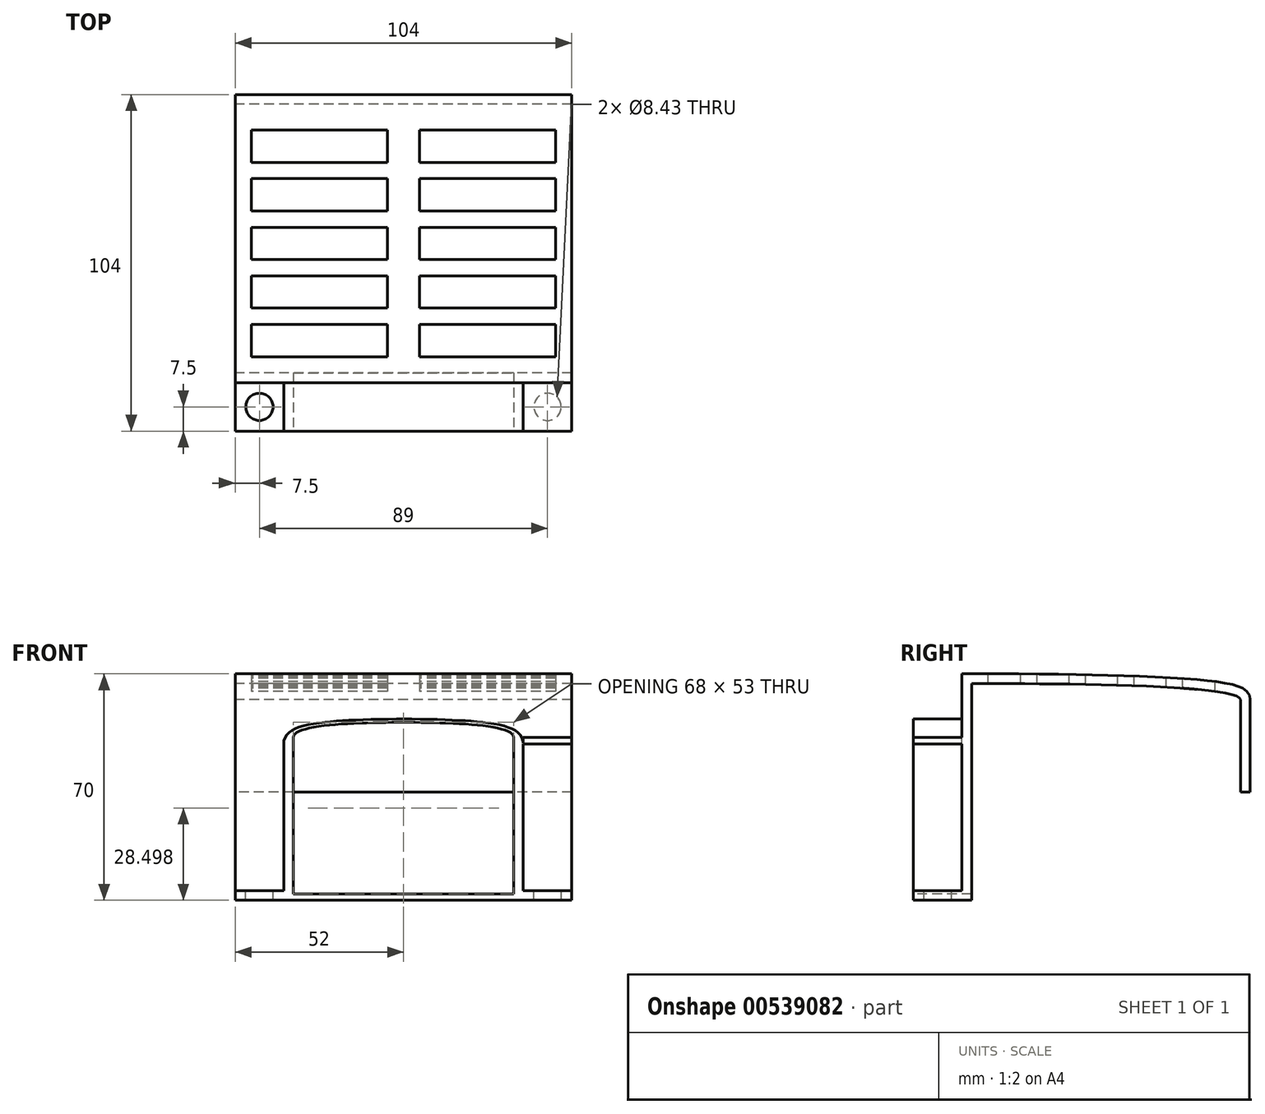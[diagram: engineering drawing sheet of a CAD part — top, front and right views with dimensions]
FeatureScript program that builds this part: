
annotation { "Feature Type Name" : "Feature", "Feature Type Description" : "" }
export const myFeature = defineFeature(function(context is Context, id is Id, definition is map)
    precondition{}
    {
        {
            var Q0;
            Q0=qCreatedBy(makeId("Right.planeOp"),FACE);
            var sketch = newSketch(context, id + "F0", { "sketchPlane" : qUnion([Q0])});
            skLineSegment(sketch, "E0", {"start": v(0, 0) * mm, "end": v(0, 67) * mm});
            skFitSpline(sketch, "E1", {"points": [v(0, 67) * mm, v(83, 62) * mm], "startDerivative": vector(81.6, 0) * mm, "endDerivative": vector(0, -13.97) * mm});
            skLineSegment(sketch, "E2", {"start": v(83, 62) * mm, "end": v(83, 33.5) * mm});
            skFitSpline(sketch, "E3.0", {"points": [v(0, 70) * mm, v(3.4, 70) * mm, v(11.1, 69.99) * mm, v(22.15, 69.91) * mm, v(31.34, 69.78) * mm, v(38.3, 69.65) * mm, v(45.17, 69.48) * mm, v(51.87, 69.25) * mm, v(58.25, 68.97) * mm, v(64.2, 68.63) * mm, v(68.7, 68.3) * mm, v(71.97, 67.98) * mm, v(74.25, 67.73) * mm, v(76.34, 67.45) * mm, v(78.23, 67.15) * mm, v(79.92, 66.82) * mm, v(81.16, 66.5) * mm, v(82.07, 66.23) * mm, v(82.72, 66) * mm, v(83.34, 65.72) * mm, v(83.95, 65.39) * mm, v(84.57, 64.95) * mm, v(85.11, 64.42) * mm, v(85.52, 63.83) * mm, v(85.78, 63.3) * mm, v(85.96, 62.67) * mm, v(86, 62.22) * mm, v(86, 62) * mm]});
            skLineSegment(sketch, "E4", {"start": v(0, 70) * mm, "end": v(-3, 70) * mm});
            skLineSegment(sketch, "E5", {"start": v(-3, 70) * mm, "end": v(-3, 0) * mm});
            skLineSegment(sketch, "E6", {"start": v(-3, 0) * mm, "end": v(0, 0) * mm});
            skLineSegment(sketch, "E7", {"start": v(86, 62) * mm, "end": v(86, 33.5) * mm});
            skLineSegment(sketch, "E8", {"start": v(86, 33.5) * mm, "end": v(83, 33.5) * mm});
            skLineSegment(sketch, "E9", {"start": v(0, 33.5) * mm, "end": v(83, 33.5) * mm, "construction": true});
            skSolve(sketch);
        }
        {
            var Q0;
            Q0 = qSketchRegion(id + "F0", true);
            extrude(context, id + "F1", {"entities" : qUnion([Q0]), "endBound" : BoundingType.SYMMETRIC, "depth" : (68 + 3 * 2 + 15 * 2) * mm, "offsetDistance" : 25 * mm});
        }
        {
            var Q0;
            Q0=makeQuery(id+"F1.opExtrude","SWEPT_FACE",FACE,{"disambiguationData":[OSD([sQuery(id+"F0.wireOp",EDGE,"E5")])]});
            var sketch = newSketch(context, id + "F2", { "sketchPlane" : qUnion([Q0])});
            skLineSegment(sketch, "E10", {"start": v(-34, 0) * mm, "end": v(-34, 50.34) * mm});
            skFitSpline(sketch, "E11", {"points": [v(-34, 50.34) * mm, v(3.6, 55) * mm], "startDerivative": vector(0, 13.97) * mm, "endDerivative": vector(37.6, 0) * mm});
            skLineSegment(sketch, "E12", {"start": v(-37, 50.34) * mm, "end": v(-37, 0) * mm});
            skLineSegment(sketch, "E13", {"start": v(-37, 0) * mm, "end": v(-34, 0) * mm});
            skLineSegment(sketch, "E14.MirrorCS", {"start": v(34, 0) * mm, "end": v(34, 50.34) * mm});
            skFitSpline(sketch, "E15.MirrorCS", {"points": [v(34, 50.34) * mm, v(-3.6, 55) * mm], "startDerivative": vector(0, 13.97) * mm, "endDerivative": vector(-37.6, 0) * mm});
            skLineSegment(sketch, "E16.MirrorCS", {"start": v(37, 50.34) * mm, "end": v(37, 0) * mm});
            skFitSpline(sketch, "E17.0", {"points": [v(37, 48.34) * mm, v(37, 48.59) * mm, v(36.96, 49.07) * mm, v(36.78, 49.77) * mm, v(36.5, 50.4) * mm, v(36.03, 51.13) * mm, v(35.35, 51.83) * mm, v(34.5, 52.44) * mm, v(33.61, 52.92) * mm, v(32.37, 53.45) * mm, v(30.68, 53.96) * mm, v(28.39, 54.45) * mm, v(25.84, 54.85) * mm, v(23.08, 55.17) * mm, v(20.14, 55.42) * mm, v(17.07, 55.61) * mm, v(12.88, 55.8) * mm, v(7.56, 55.95) * mm, v(1.5, 56) * mm, v(-2.04, 56) * mm, v(-3.6, 56) * mm]});
            skFitSpline(sketch, "E17.1", {"points": [v(-37, 48.34) * mm, v(-37, 48.59) * mm, v(-36.96, 49.07) * mm, v(-36.78, 49.77) * mm, v(-36.5, 50.4) * mm, v(-36.03, 51.13) * mm, v(-35.35, 51.83) * mm, v(-34.5, 52.44) * mm, v(-33.61, 52.92) * mm, v(-32.37, 53.45) * mm, v(-30.68, 53.96) * mm, v(-28.39, 54.45) * mm, v(-25.84, 54.85) * mm, v(-23.08, 55.17) * mm, v(-20.14, 55.42) * mm, v(-17.07, 55.61) * mm, v(-12.88, 55.8) * mm, v(-7.56, 55.95) * mm, v(-1.5, 56) * mm, v(2.04, 56) * mm, v(3.6, 56) * mm]});
            skLineSegment(sketch, "E18.MirrorCS", {"start": v(37, 0) * mm, "end": v(34, 0) * mm});
            skSolve(sketch);
        }
        {
            var Q0;
            Q0 = qSketchRegion(id + "F2", true);
            extrude(context, id + "F3", {"entities" : qUnion([Q0]), "operationType" : NewBodyOperationType.ADD, "depth" : 15 * mm, "offsetDistance" : 25 * mm});
        }
        {
            var Q0;
            Q0=makeQuery(id+"F3.boolean.opBoolean","SPLIT",FACE,{"disambiguationData":[TD([makeQuery(id+"F3.opExtrude","SWEPT_FACE",FACE,{"disambiguationData":[OSD([sQuery(id+"F2.wireOp",EDGE,"E10")])]})])],"derivedFrom":makeQuery(id+"F1.opExtrude","SWEPT_FACE",FACE,{"disambiguationData":[OSD([sQuery(id+"F0.wireOp",EDGE,"E5")])]})});
            var Q1;
            Q1=makeQuery(id+"F1.opExtrude","SWEPT_FACE",FACE,{"disambiguationData":[OSD([sQuery(id+"F0.wireOp",EDGE,"E0")])]});
            extrude(context, id + "F4", {"entities" : qUnion([Q0]), "operationType" : NewBodyOperationType.REMOVE, "endBound" : BoundingType.UP_TO_SURFACE, "oppositeDirection" : true, "depth" : 25 * mm, "endBoundEntityFace" : qUnion([Q1]), "offsetDistance" : 25 * mm});
        }
        {
            var Q0;
            Q0=makeQuery(id+"F3.opExtrude","SWEPT_FACE",FACE,{"disambiguationData":[OSD([sQuery(id+"F2.wireOp",EDGE,"E16.MirrorCS")])]});
            var sketch = newSketch(context, id + "F5", { "sketchPlane" : qUnion([Q0])});
            skLineSegment(sketch, "E19.bottom", {"start": v(-18, 0) * mm, "end": v(-3, 0) * mm});
            skLineSegment(sketch, "E19.top", {"start": v(-18, 3) * mm, "end": v(-3, 3) * mm});
            skLineSegment(sketch, "E19.left", {"start": v(-18, 0) * mm, "end": v(-18, 3) * mm});
            skLineSegment(sketch, "E19.right", {"start": v(-3, 0) * mm, "end": v(-3, 3) * mm});
            skSolve(sketch);
        }
        {
            var Q0;
            Q0 = qSketchRegion(id + "F5", true);
            var Q1;
            Q1=makeQuery(id+"F0N0LtJJwjJDzAm_1.boolean.opBoolean","MERGE",FACE,{"derivedFrom":[makeQuery(id+"F1.opExtrude","CAP_FACE",FACE,{"disambiguationData":[OSD([sQuery(id+"F0.wireOp",EDGE,"E0"),sQuery(id+"F0.wireOp",EDGE,"E1"),sQuery(id+"F0.wireOp",EDGE,"E2"),sQuery(id+"F0.wireOp",EDGE,"E3.0"),sQuery(id+"F0.wireOp",EDGE,"E4"),sQuery(id+"F0.wireOp",EDGE,"E5"),sQuery(id+"F0.wireOp",EDGE,"E6"),sQuery(id+"F0.wireOp",EDGE,"E7"),sQuery(id+"F0.wireOp",EDGE,"E8")])],"isStart":false}),makeQuery(id+"F0N0LtJJwjJDzAm_1.opExtrude","SWEPT_FACE",FACE,{"disambiguationData":[OSD([sQuery(id+"FstOfnZHvo9ash0_1.wireOp",EDGE,"mnMYi594-UZgm-Wnls-jQ8F-WkxtBhiRCk1N.left")])]})]});
            var Q2;
            Q2=makeQuery(id+"F1.opExtrude","CAP_VERTEX",VERTEX,{"disambiguationData":[OSD([sQuery(id+"F0.wireOp",EDGE,"E5"),sQuery(id+"F0.wireOp",EDGE,"E6")])],"isStart":false});
            extrude(context, id + "F6", {"entities" : qUnion([Q0]), "operationType" : NewBodyOperationType.ADD, "endBound" : BoundingType.UP_TO_VERTEX, "depth" : 4 * mm, "endBoundEntityFace" : qUnion([Q1]), "endBoundEntityVertex" : qUnion([Q2]), "offsetDistance" : 25 * mm});
        }
        {
            var Q0;
            Q0=makeQuery(id+"F3.opExtrude","SWEPT_FACE",FACE,{"disambiguationData":[OSD([sQuery(id+"F2.wireOp",EDGE,"E12")])]});
            var sketch = newSketch(context, id + "F7", { "sketchPlane" : qUnion([Q0])});
            skLineSegment(sketch, "E20.bottom", {"start": v(18, 0) * mm, "end": v(3, 0) * mm});
            skLineSegment(sketch, "E20.top", {"start": v(18, 3) * mm, "end": v(3, 3) * mm});
            skLineSegment(sketch, "E20.left", {"start": v(18, 0) * mm, "end": v(18, 3) * mm});
            skLineSegment(sketch, "E20.right", {"start": v(3, 0) * mm, "end": v(3, 3) * mm});
            skSolve(sketch);
        }
        {
            var Q0;
            Q0 = qSketchRegion(id + "F7", true);
            var Q1;
            Q1=makeQuery(id+"F1.opExtrude","CAP_VERTEX",VERTEX,{"disambiguationData":[OSD([sQuery(id+"F0.wireOp",EDGE,"E5"),sQuery(id+"F0.wireOp",EDGE,"E6")])],"isStart":true});
            extrude(context, id + "F8", {"entities" : qUnion([Q0]), "operationType" : NewBodyOperationType.ADD, "endBound" : BoundingType.UP_TO_VERTEX, "depth" : 25 * mm, "endBoundEntityVertex" : qUnion([Q1]), "offsetDistance" : 25 * mm});
        }
        {
            var Q0;
            Q0=makeQuery(id+"F6.opExtrude","SWEPT_FACE",FACE,{"disambiguationData":[OSD([sQuery(id+"F5.wireOp",EDGE,"E19.top")])]});
            var sketch = newSketch(context, id + "F9", { "sketchPlane" : qUnion([Q0])});
            skPoint(sketch, "E21", {"position": v(44.5, -10.5) * mm});
            skLineSegment(sketch, "E22", {"start": v(44.5, -18) * mm, "end": v(44.5, -3) * mm, "construction": true});
            skSolve(sketch);
        }
        {
            var Q0;
            Q0=makeQuery(id+"F8.opExtrude","SWEPT_FACE",FACE,{"disambiguationData":[OSD([sQuery(id+"F7.wireOp",EDGE,"E20.top")])]});
            var sketch = newSketch(context, id + "F10", { "sketchPlane" : qUnion([Q0])});
            skPoint(sketch, "E23", {"position": v(-44.5, -10.5) * mm});
            skLineSegment(sketch, "E24", {"start": v(-44.5, -18) * mm, "end": v(-44.5, -3) * mm, "construction": true});
            skSolve(sketch);
        }
        {
            var Q0;
            Q0=sQuery(id+"F10.wireOp",VERTEX,"E23");
            var Q1;
            Q1=sQuery(id+"F9.wireOp",VERTEX,"E21");
            var Q2;
            Q2=makeQuery(id+"F1.opExtrude","SWEPT_BODY",BODY,{"disambiguationData":[OSD([sQuery(id+"F0.wireOp",EDGE,"E0"),sQuery(id+"F0.wireOp",EDGE,"E1"),sQuery(id+"F0.wireOp",EDGE,"E2"),sQuery(id+"F0.wireOp",EDGE,"E3.0"),sQuery(id+"F0.wireOp",EDGE,"E4"),sQuery(id+"F0.wireOp",EDGE,"E5"),sQuery(id+"F0.wireOp",EDGE,"E6"),sQuery(id+"F0.wireOp",EDGE,"E7"),sQuery(id+"F0.wireOp",EDGE,"E8")])]});
            hole(context, id + "F11", {"style" : HoleStyle.SIMPLE, "endStyle" : HoleEndStyle.THROUGH, "standardTappedOrClearance" : lookupTablePath({ "standard" : "ANSI", "fit" : "Normal (ASME)", "size" : "5/16", "type" : "Clearance" }), "standardBlindInLast" : lookupTablePath({ "fit" : "Free", "standard" : "ANSI", "size" : "5/16", "type" : "Clearance" }), "holeDiameter" : 8.43 * mm, "isTappedThrough" : true, "tappedDepth" : 12 * mm, "tapClearance" : 3, "locations" : qUnion([Q0, Q1]), "scope" : qUnion([Q2])});
        }
        {
            var Q0;
            Q0=qCreatedBy(makeId("Top.planeOp"),FACE);
            var sketch = newSketch(context, id + "F12", { "sketchPlane" : qUnion([Q0])});
            skLineSegment(sketch, "E25.bottom", {"start": v(5, 5) * mm, "end": v(47, 5) * mm});
            skLineSegment(sketch, "E25.top", {"start": v(5, 15) * mm, "end": v(47, 15) * mm});
            skLineSegment(sketch, "E25.left", {"start": v(5, 5) * mm, "end": v(5, 15) * mm});
            skLineSegment(sketch, "E25.right", {"start": v(47, 5) * mm, "end": v(47, 15) * mm});
            skLineSegment(sketch, "E26.MirrorCS", {"start": v(-5, 15) * mm, "end": v(-47, 15) * mm});
            skLineSegment(sketch, "E27.MirrorCS", {"start": v(-5, 5) * mm, "end": v(-5, 15) * mm});
            skLineSegment(sketch, "E28.MirrorCS", {"start": v(-5, 5) * mm, "end": v(-47, 5) * mm});
            skLineSegment(sketch, "E29.MirrorCS", {"start": v(-47, 5) * mm, "end": v(-47, 15) * mm});
            skLineSegment(sketch, "E30.0.1.0", {"start": v(-5, 30) * mm, "end": v(-47, 30) * mm});
            skLineSegment(sketch, "E30.0.1.1", {"start": v(-47, 20) * mm, "end": v(-47, 30) * mm});
            skLineSegment(sketch, "E30.0.1.2", {"start": v(-5, 20) * mm, "end": v(-47, 20) * mm});
            skLineSegment(sketch, "E30.0.1.3", {"start": v(-5, 20) * mm, "end": v(-5, 30) * mm});
            skLineSegment(sketch, "E30.0.1.4", {"start": v(5, 30) * mm, "end": v(47, 30) * mm});
            skLineSegment(sketch, "E30.0.1.5", {"start": v(5, 20) * mm, "end": v(5, 30) * mm});
            skLineSegment(sketch, "E30.0.1.6", {"start": v(5, 20) * mm, "end": v(47, 20) * mm});
            skLineSegment(sketch, "E30.0.1.7", {"start": v(47, 20) * mm, "end": v(47, 30) * mm});
            skLineSegment(sketch, "E30.0.2.0", {"start": v(-5, 45) * mm, "end": v(-47, 45) * mm});
            skLineSegment(sketch, "E30.0.2.1", {"start": v(-47, 35) * mm, "end": v(-47, 45) * mm});
            skLineSegment(sketch, "E30.0.2.2", {"start": v(-5, 35) * mm, "end": v(-47, 35) * mm});
            skLineSegment(sketch, "E30.0.2.3", {"start": v(-5, 35) * mm, "end": v(-5, 45) * mm});
            skLineSegment(sketch, "E30.0.2.4", {"start": v(5, 45) * mm, "end": v(47, 45) * mm});
            skLineSegment(sketch, "E30.0.2.5", {"start": v(5, 35) * mm, "end": v(5, 45) * mm});
            skLineSegment(sketch, "E30.0.2.6", {"start": v(5, 35) * mm, "end": v(47, 35) * mm});
            skLineSegment(sketch, "E30.0.2.7", {"start": v(47, 35) * mm, "end": v(47, 45) * mm});
            skLineSegment(sketch, "E30.0.3.0", {"start": v(-5, 60) * mm, "end": v(-47, 60) * mm});
            skLineSegment(sketch, "E30.0.3.1", {"start": v(-47, 50) * mm, "end": v(-47, 60) * mm});
            skLineSegment(sketch, "E30.0.3.2", {"start": v(-5, 50) * mm, "end": v(-47, 50) * mm});
            skLineSegment(sketch, "E30.0.3.3", {"start": v(-5, 50) * mm, "end": v(-5, 60) * mm});
            skLineSegment(sketch, "E30.0.3.4", {"start": v(5, 60) * mm, "end": v(47, 60) * mm});
            skLineSegment(sketch, "E30.0.3.5", {"start": v(5, 50) * mm, "end": v(5, 60) * mm});
            skLineSegment(sketch, "E30.0.3.6", {"start": v(5, 50) * mm, "end": v(47, 50) * mm});
            skLineSegment(sketch, "E30.0.3.7", {"start": v(47, 50) * mm, "end": v(47, 60) * mm});
            skLineSegment(sketch, "E30.0.4.0", {"start": v(-5, 75) * mm, "end": v(-47, 75) * mm});
            skLineSegment(sketch, "E30.0.4.1", {"start": v(-47, 65) * mm, "end": v(-47, 75) * mm});
            skLineSegment(sketch, "E30.0.4.2", {"start": v(-5, 65) * mm, "end": v(-47, 65) * mm});
            skLineSegment(sketch, "E30.0.4.3", {"start": v(-5, 65) * mm, "end": v(-5, 75) * mm});
            skLineSegment(sketch, "E30.0.4.4", {"start": v(5, 75) * mm, "end": v(47, 75) * mm});
            skLineSegment(sketch, "E30.0.4.5", {"start": v(5, 65) * mm, "end": v(5, 75) * mm});
            skLineSegment(sketch, "E30.0.4.6", {"start": v(5, 65) * mm, "end": v(47, 65) * mm});
            skLineSegment(sketch, "E30.0.4.7", {"start": v(47, 65) * mm, "end": v(47, 75) * mm});
            skLineSegment(sketch, "E30.direction1", {"start": v(-47, 5) * mm, "end": v(-22, 5) * mm, "construction": true});
            skLineSegment(sketch, "E30.direction2", {"start": v(-47, 5) * mm, "end": v(-47, 20) * mm, "construction": true});
            skSolve(sketch);
        }
        {
            var Q0;
            Q0 = qSketchRegion(id + "F12", true);
            extrude(context, id + "F13", {"entities" : qUnion([Q0]), "operationType" : NewBodyOperationType.REMOVE, "endBound" : BoundingType.THROUGH_ALL, "depth" : 25 * mm, "offsetDistance" : 25 * mm});
        }
        {
            var Q0;
            Q0=makeQuery(id+"F3.opExtrude","SWEPT_FACE",FACE,{"disambiguationData":[OSD([sQuery(id+"F2.wireOp",EDGE,"E16.MirrorCS")])]});
            var sketch = newSketch(context, id + "F14", { "sketchPlane" : qUnion([Q0])});
            skLineSegment(sketch, "E31.bottom", {"start": v(-3, 50.34) * mm, "end": v(-18, 50.34) * mm});
            skLineSegment(sketch, "E31.top", {"start": v(-3, 48.34) * mm, "end": v(-18, 48.34) * mm});
            skLineSegment(sketch, "E31.left", {"start": v(-3, 50.34) * mm, "end": v(-3, 48.34) * mm});
            skLineSegment(sketch, "E31.right", {"start": v(-18, 50.34) * mm, "end": v(-18, 48.34) * mm});
            skSolve(sketch);
        }
        {
            var Q0;
            Q0 = qSketchRegion(id + "F14", true);
            var Q1;
            Q1=makeQuery(id+"F6.boolean.opBoolean","MERGE",FACE,{"derivedFrom":[makeQuery(id+"F1.opExtrude","CAP_FACE",FACE,{"disambiguationData":[OSD([sQuery(id+"F0.wireOp",EDGE,"E0"),sQuery(id+"F0.wireOp",EDGE,"E1"),sQuery(id+"F0.wireOp",EDGE,"E2"),sQuery(id+"F0.wireOp",EDGE,"E3.0"),sQuery(id+"F0.wireOp",EDGE,"E4"),sQuery(id+"F0.wireOp",EDGE,"E5"),sQuery(id+"F0.wireOp",EDGE,"E6"),sQuery(id+"F0.wireOp",EDGE,"E7"),sQuery(id+"F0.wireOp",EDGE,"E8")])],"isStart":false}),makeQuery(id+"F6.opExtrude","CAP_FACE",FACE,{"disambiguationData":[OSD([dummyQuery(id+"F6.vertexPlane.planeOp",FACE)])],"isStart":false})]});
            extrude(context, id + "F15", {"entities" : qUnion([Q0]), "operationType" : NewBodyOperationType.ADD, "endBound" : BoundingType.UP_TO_SURFACE, "depth" : 25 * mm, "endBoundEntityFace" : qUnion([Q1]), "offsetDistance" : 25 * mm});
        }
        {
            var Q0;
            {var subQ0=sQuery(id+"F2.wireOp",EDGE,"E14.MirrorCS");Q0=makeQuery(id+"F4.boolean.opBoolean","MERGE",FACE,{"derivedFrom":[makeQuery(id+"F3.opExtrude","SWEPT_FACE",FACE,{"disambiguationData":[OSD([subQ0])]}),makeQuery(id+"F4.opExtrude","SWEPT_FACE",FACE,{"disambiguationData":[OSD([subQ0])]})]});}
            var sketch = newSketch(context, id + "F16", { "sketchPlane" : qUnion([Q0])});
            skLineSegment(sketch, "E32.bottom", {"start": v(0, 0) * mm, "end": v(18, 0) * mm});
            skLineSegment(sketch, "E32.top", {"start": v(0, 2) * mm, "end": v(18, 2) * mm});
            skLineSegment(sketch, "E32.left", {"start": v(0, 0) * mm, "end": v(0, 2) * mm});
            skLineSegment(sketch, "E32.right", {"start": v(18, 0) * mm, "end": v(18, 2) * mm});
            skSolve(sketch);
        }
        {
            var Q0;
            Q0 = qSketchRegion(id + "F16", true);
            var Q1;
            {var subQ0=sQuery(id+"F2.wireOp",EDGE,"E10");Q1=makeQuery(id+"F4.boolean.opBoolean","MERGE",FACE,{"derivedFrom":[makeQuery(id+"F3.opExtrude","SWEPT_FACE",FACE,{"disambiguationData":[OSD([subQ0])]}),makeQuery(id+"F4.opExtrude","SWEPT_FACE",FACE,{"disambiguationData":[OSD([subQ0])]})]});}
            extrude(context, id + "F17", {"entities" : qUnion([Q0]), "operationType" : NewBodyOperationType.ADD, "endBound" : BoundingType.UP_TO_SURFACE, "depth" : 25 * mm, "endBoundEntityFace" : qUnion([Q1]), "offsetDistance" : 25 * mm});
        }
    });
